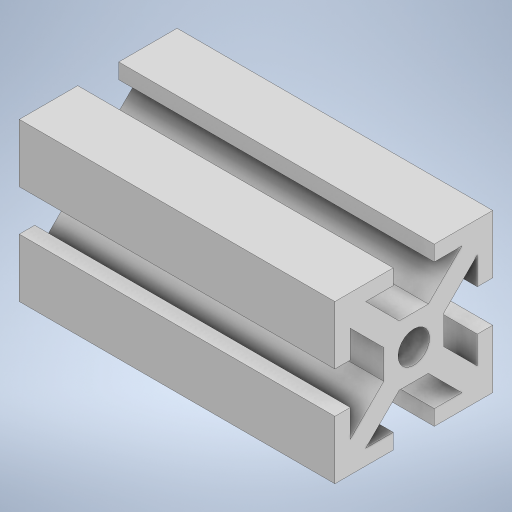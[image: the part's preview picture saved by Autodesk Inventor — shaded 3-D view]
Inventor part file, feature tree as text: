
AUTODESK INVENTOR PART (.ipt)
format: ipt  version: 2023 (Build 270158030, 158C)  size: 258,560 bytes
history: native  units: in
note: dims shown in document units (in); Inventor stores cm internally (conversion verified against a paired STEP export)
features: extrude x1, sketch x1
ambient origin geometry x8: Origin, YZ Plane, XZ Plane, XY Plane, X Axis, Y Axis, Z Axis, Center Point
bodies: Solid1 (feature_tree)
feature tree (2):
  extrude  "Extrusion1"  Depth=0.0975in
  sketch  "Sketch1"  dims[d2=0.37in d3=0.0975in d7=0.0975in d10=0.0975in d11=1.0in d13=0.0975in d16=0.0975in d17=0.37in d18=1.0in d23=0.0975in d24=1.0in d25=1.0in d32=0.175in d33=0.175in d35=135.0deg d36=0.175in d37=0.175in d38=0.0975in d40=0.175in d41=0.175in d42=0.175in d43=0.175in d44=0.2in d45=2.0in d46=0.0in]
